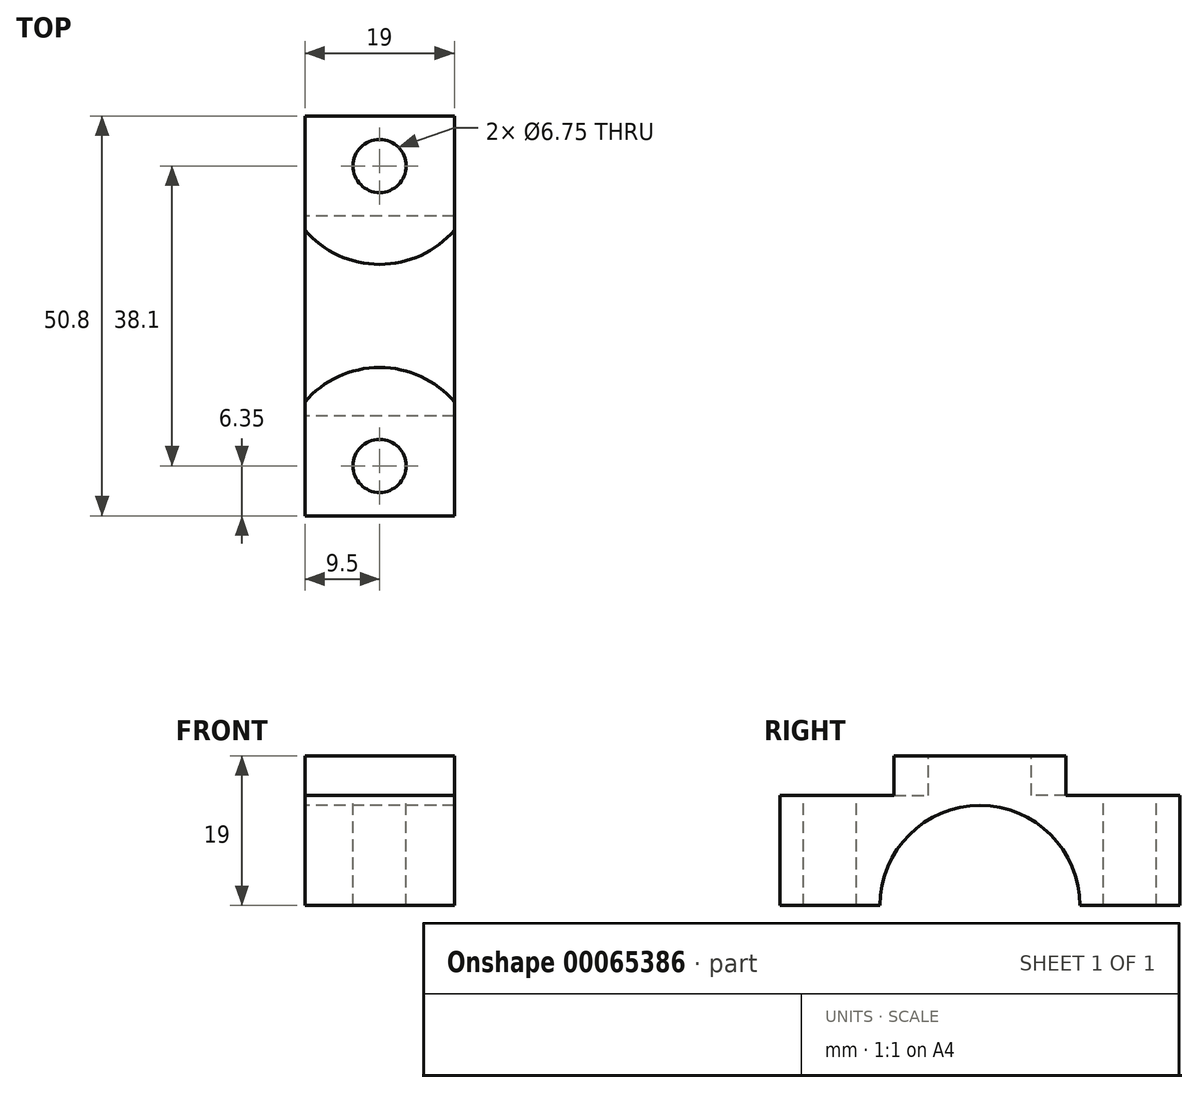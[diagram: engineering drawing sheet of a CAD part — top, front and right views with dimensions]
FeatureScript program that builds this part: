
annotation { "Feature Type Name" : "Feature", "Feature Type Description" : "" }
export const myFeature = defineFeature(function(context is Context, id is Id, definition is map)
    precondition{}
    {
        {
            var Q0;
            Q0=qCreatedBy(makeId("Right.planeOp"),FACE);
            var sketch = newSketch(context, id + "F0", { "sketchPlane" : qUnion([Q0])});
            skLineSegment(sketch, "E0.bottom", {"start": v(-25.4, 19) * mm, "end": v(25.4, 19) * mm});
            skLineSegment(sketch, "E0.top", {"start": v(-25.4, 0) * mm, "end": v(25.4, 0) * mm});
            skLineSegment(sketch, "E0.left", {"start": v(-25.4, 19) * mm, "end": v(-25.4, 0) * mm});
            skLineSegment(sketch, "E0.right", {"start": v(25.4, 19) * mm, "end": v(25.4, 0) * mm});
            skCircle(sketch, "E1", {"center": v(0, 0) * mm, "radius": 12.7 * mm});
            skSolve(sketch);
        }
        {
            var Q0;
            Q0=makeQuery(id+"F0.imprint","IMPRINT",FACE,{"disambiguationData":[TD([[makeQuery(id+"F0.imprint","IMPRINT",EDGE,{"derivedFrom":sQuery(id+"F0.wireOp",EDGE,"E0.bottom")}),-1.0]])]});
            extrude(context, id + "F1", {"entities" : qUnion([Q0]), "endBound" : BoundingType.SYMMETRIC, "depth" : 19 * mm});
        }
        {
            var Q0;
            Q0=makeQuery(id+"F1.opExtrude","SWEPT_FACE",FACE,{"disambiguationData":[OSD([sQuery(id+"F0.wireOp",EDGE,"E0.bottom")])]});
            var sketch = newSketch(context, id + "F2", { "sketchPlane" : qUnion([Q0])});
            skPoint(sketch, "E2", {"position": v(0, 19.05) * mm});
            skPoint(sketch, "E3", {"position": v(0, -19.05) * mm});
            skSolve(sketch);
        }
        {
            var Q0;
            Q0=sQuery(id+"F2.wireOp",VERTEX,"E2");
            var Q1;
            Q1=sQuery(id+"F2.wireOp",VERTEX,"E3");
            var Q2;
            Q2=makeQuery(id+"F1.opExtrude","SWEPT_BODY",BODY,{"disambiguationData":[OSD([sQuery(id+"F0.wireOp",EDGE,"E0.bottom"),sQuery(id+"F0.wireOp",EDGE,"E0.top"),sQuery(id+"F0.wireOp",EDGE,"E0.left"),sQuery(id+"F0.wireOp",EDGE,"E0.right"),sQuery(id+"F0.wireOp",EDGE,"E1")])]});
            hole(context, id + "F3", {"style" : HoleStyle.C_BORE, "holeDiameter" : 6.75 * mm, "cBoreDiameter" : 25 * mm, "cBoreDepth" : 5 * mm, "endStyle" : HoleEndStyle.THROUGH, "locations" : qUnion([Q0, Q1]), "scope" : qUnion([Q2])});
        }
    });
